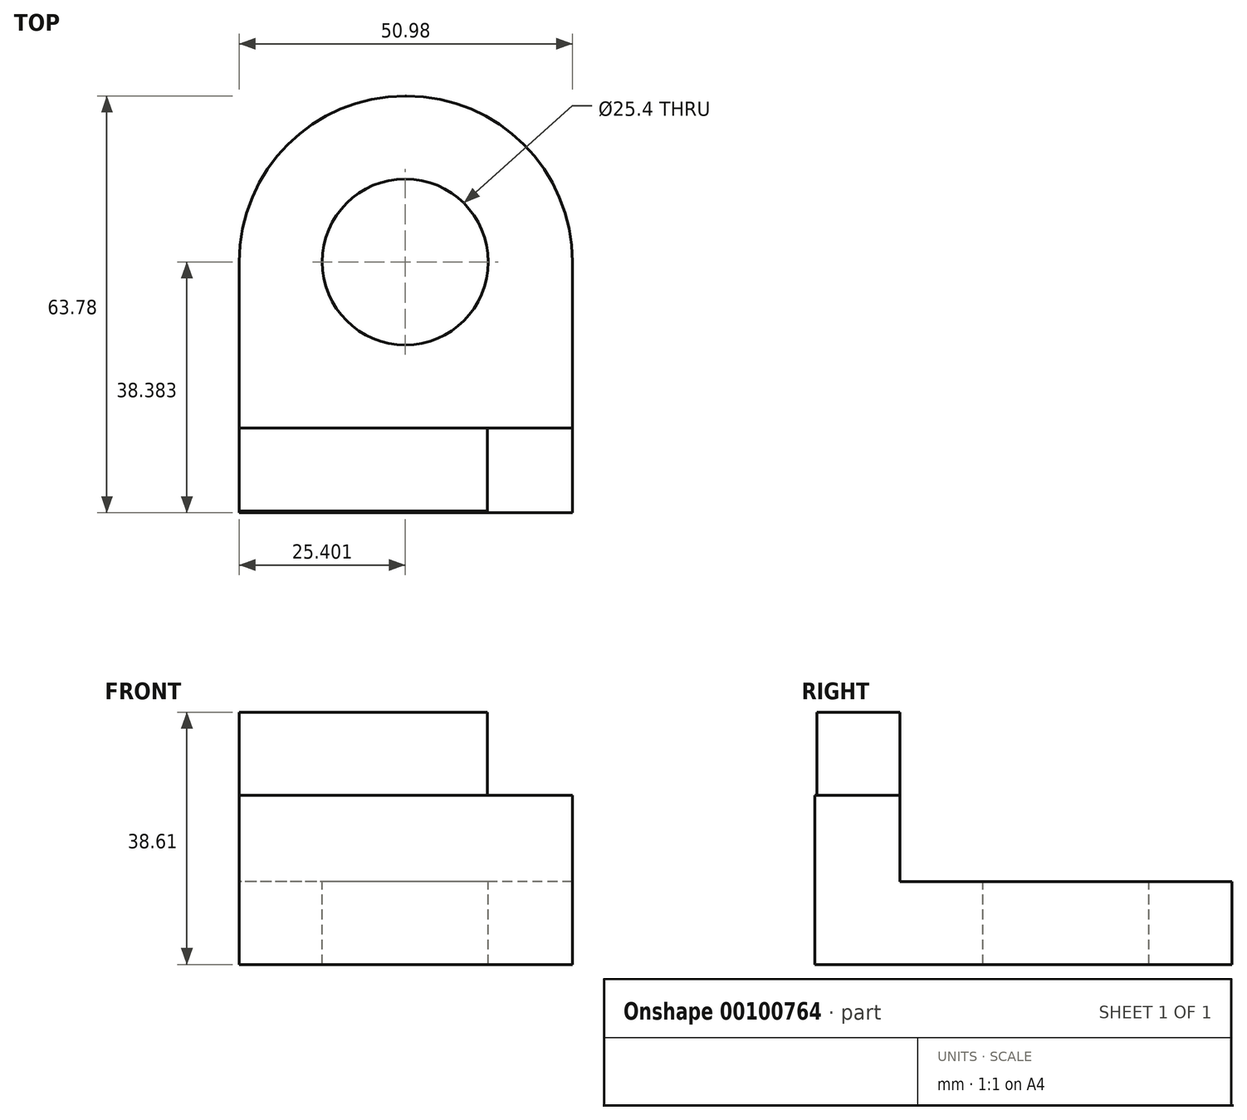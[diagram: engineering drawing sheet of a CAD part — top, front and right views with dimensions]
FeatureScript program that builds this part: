
annotation { "Feature Type Name" : "Feature", "Feature Type Description" : "" }
export const myFeature = defineFeature(function(context is Context, id is Id, definition is map)
    precondition{}
    {
        {
            var Q0;
            Q0=qCreatedBy(makeId("Right.planeOp"),FACE);
            var sketch = newSketch(context, id + "F0", { "sketchPlane" : qUnion([Q0])});
            skLineSegment(sketch, "E0.bottom", {"start": v(36.7, 17.37) * mm, "end": v(23.71, 17.37) * mm});
            skLineSegment(sketch, "E0.top", {"start": v(36.7, -8.54) * mm, "end": v(23.71, -8.54) * mm});
            skLineSegment(sketch, "E0.left", {"start": v(36.7, 17.37) * mm, "end": v(36.7, -8.54) * mm});
            skLineSegment(sketch, "E0.right", {"start": v(23.71, 17.37) * mm, "end": v(23.71, -8.54) * mm});
            skSolve(sketch);
        }
        {
            var Q0;
            Q0=makeQuery(id+"F0.imprint","IMPRINT",FACE,{"disambiguationData":[TD([[makeQuery(id+"F0.imprint","IMPRINT",EDGE,{"derivedFrom":sQuery(id+"F0.wireOp",EDGE,"E0.bottom")}),1.0]])]});
            extrude(context, id + "F1", {"entities" : qUnion([Q0]), "endBound" : BoundingType.SYMMETRIC, "depth" : 50.98 * mm});
        }
        {
            var Q0;
            Q0=qCreatedBy(makeId("Front.planeOp"),FACE);
            var sketch = newSketch(context, id + "F2", { "sketchPlane" : qUnion([Q0])});
            skLineSegment(sketch, "E1.bottom", {"start": v(-12.66, 17.48) * mm, "end": v(25.44, 17.48) * mm});
            skLineSegment(sketch, "E1.top", {"start": v(-12.66, 30.18) * mm, "end": v(25.44, 30.18) * mm});
            skLineSegment(sketch, "E1.left", {"start": v(-12.66, 17.48) * mm, "end": v(-12.66, 30.18) * mm});
            skLineSegment(sketch, "E1.right", {"start": v(25.44, 17.48) * mm, "end": v(25.44, 30.18) * mm});
            skSolve(sketch);
        }
        {
            var Q0;
            Q0=makeQuery(id+"F2.imprint","IMPRINT",FACE,{"disambiguationData":[TD([[makeQuery(id+"F2.imprint","IMPRINT",EDGE,{"derivedFrom":sQuery(id+"F2.wireOp",EDGE,"E1.bottom")}),1.0]])]});
            extrude(context, id + "F3", {"entities" : qUnion([Q0]), "endBound" : BoundingType.SYMMETRIC, "depth" : 12.7 * mm});
        }
        {
            var Q0;
            Q0=makeQuery(id+"F1.opExtrude","SWEPT_FACE",FACE,{"disambiguationData":[OSD([sQuery(id+"F0.wireOp",EDGE,"E0.bottom")])]});
            var sketch = newSketch(context, id + "F4", { "sketchPlane" : qUnion([Q0])});
            skSolve(sketch);
        }
        {
            var Q0;
            Q0=makeQuery(id+"F3.opExtrude","SWEPT_BODY",BODY,{"disambiguationData":[OSD([sQuery(id+"F2.wireOp",EDGE,"E1.bottom"),sQuery(id+"F2.wireOp",EDGE,"E1.top"),sQuery(id+"F2.wireOp",EDGE,"E1.left"),sQuery(id+"F2.wireOp",EDGE,"E1.right")])]});
            deleteBodies(context, id + "F5", {"entities" : qUnion([Q0])});
        }
        {
            var Q0;
            {var subQ0=sQuery(id+"F0.wireOp",EDGE,"E0.bottom");Q0=makeQuery(id+"F4.imprint","IMPRINT",FACE,{"disambiguationData":[TD([[makeQuery(id+"F4.imprint","IMPRINT",EDGE,{"derivedFrom":makeQuery(id+"F1.opExtrude","CAP_EDGE",EDGE,{"disambiguationData":[OSD([subQ0])],"isStart":true})}),1.0]])]});}
            var sketch = newSketch(context, id + "F6", { "sketchPlane" : qUnion([Q0])});
            skLineSegment(sketch, "E2.bottom", {"start": v(-25.64, 36.71) * mm, "end": v(12.46, 36.71) * mm});
            skLineSegment(sketch, "E2.top", {"start": v(-25.64, 24.01) * mm, "end": v(12.46, 24.01) * mm});
            skLineSegment(sketch, "E2.left", {"start": v(-25.64, 36.71) * mm, "end": v(-25.64, 24.01) * mm});
            skLineSegment(sketch, "E2.right", {"start": v(12.46, 36.71) * mm, "end": v(12.46, 24.01) * mm});
            skSolve(sketch);
        }
        {
            var Q0;
            {var subQ0=sQuery(id+"F6.wireOp",EDGE,"E2.right");var subQ1=sQuery(id+"F6.wireOp",EDGE,"E2.top");var subQ2=makeQuery(id+"F6.imprint","INTERSECT",VERTEX,{"derivedFrom":[subQ1,subQ0]});Q0=makeQuery(id+"F6.imprint","IMPRINT",FACE,{"disambiguationData":[TD([[makeQuery(id+"F6.imprint","IMPRINT",EDGE,{"disambiguationData":[TD([[subQ2,1.0]])],"derivedFrom":subQ1}),1.0]])]});}
            extrude(context, id + "F7", {"entities" : qUnion([Q0]), "operationType" : NewBodyOperationType.ADD, "depth" : 12.7 * mm});
        }
        {
            var Q0;
            {var subQ0=sQuery(id+"F0.wireOp",EDGE,"E0.left");Q0=makeQuery(id+"F7.boolean.opBoolean","MERGE",FACE,{"derivedFrom":[makeQuery(id+"F1.opExtrude","SWEPT_FACE",FACE,{"disambiguationData":[OSD([subQ0])]}),makeQuery(id+"F7.opExtrude","SWEPT_FACE",FACE,{"disambiguationData":[OSD([sQuery(id+"F0.wireOp",EDGE,"E0.bottom"),subQ0])]})]});}
            var sketch = newSketch(context, id + "F8", { "sketchPlane" : qUnion([Q0])});
            skLineSegment(sketch, "E3.bottom", {"start": v(-25.49, 4.16) * mm, "end": v(25.49, 4.16) * mm});
            skLineSegment(sketch, "E3.top", {"start": v(-25.49, -8.54) * mm, "end": v(25.49, -8.54) * mm});
            skLineSegment(sketch, "E3.left", {"start": v(-25.49, 4.16) * mm, "end": v(-25.49, -8.54) * mm});
            skLineSegment(sketch, "E3.right", {"start": v(25.49, 4.16) * mm, "end": v(25.49, -8.54) * mm});
            skSolve(sketch);
        }
        {
            var Q0;
            Q0=makeQuery(id+"F8.imprint","IMPRINT",FACE,{"disambiguationData":[TD([[makeQuery(id+"F8.imprint","IMPRINT",EDGE,{"derivedFrom":sQuery(id+"F8.wireOp",EDGE,"E3.bottom")}),-1.0]])]});
            extrude(context, id + "F9", {"entities" : qUnion([Q0]), "operationType" : NewBodyOperationType.ADD, "depth" : 50.8 * mm});
        }
        {
            var Q0;
            Q0=makeQuery(id+"F9.opExtrude","SWEPT_FACE",FACE,{"disambiguationData":[OSD([sQuery(id+"F8.wireOp",EDGE,"E3.bottom")])]});
            var sketch = newSketch(context, id + "F10", { "sketchPlane" : qUnion([Q0])});
            skCircle(sketch, "E4", {"center": v(-0.09, 62.1) * mm, "radius": 12.7 * mm});
            skSolve(sketch);
        }
        {
            var Q0;
            Q0=makeQuery(id+"F10.imprint","IMPRINT",FACE,{"disambiguationData":[TD([[makeQuery(id+"F10.imprint","IMPRINT",EDGE,{"derivedFrom":sQuery(id+"F10.wireOp",EDGE,"E4")}),1.0]])]});
            extrude(context, id + "F11", {"entities" : qUnion([Q0]), "operationType" : NewBodyOperationType.REMOVE, "endBound" : BoundingType.THROUGH_ALL, "oppositeDirection" : true, "depth" : 25.4 * mm});
        }
        {
            var Q0;
            Q0=makeQuery(id+"F9.opExtrude","CAP_EDGE",EDGE,{"disambiguationData":[OSD([sQuery(id+"F8.wireOp",EDGE,"E3.right")])],"isStart":false});
            var Q1;
            Q1=makeQuery(id+"F9.opExtrude","CAP_EDGE",EDGE,{"disambiguationData":[OSD([sQuery(id+"F8.wireOp",EDGE,"E3.left")])],"isStart":false});
            fillet(context, id + "F12", {"entities" : qUnion([Q0, Q1]), "radius" : 25.4 * mm, "tangentPropagation" : true, "allowEdgeOverflow" : false});
        }
    });
